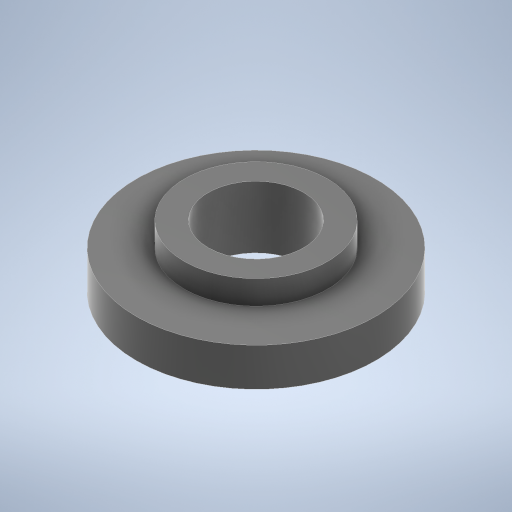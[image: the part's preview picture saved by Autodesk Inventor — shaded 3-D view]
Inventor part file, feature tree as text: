
AUTODESK INVENTOR PART (.ipt)
format: ipt  version: 2024.2 (Build 282272000, 272)  size: 245,760 bytes
history: native  units: mm
features: revolve x1, sketch x1
ambient origin geometry x8: Origin, YZ Plane, XZ Plane, XY Plane, X Axis, Y Axis, Z Axis, Center Point
bodies: Solid1 (feature_tree)
feature tree (2):
  revolve  "Revolution1"  [1 undecoded]
  sketch  "Sketch1"  dims[d0=2.0mm d1=3.0mm d2=5.0mm d3=0.8mm d4=0.5mm d5=90.0deg]
note: 1 required parameter value undecoded (feature->parameter linkage not recoverable at this tier; creation-order binding heuristic only, values carry confidence <= 0.55)
